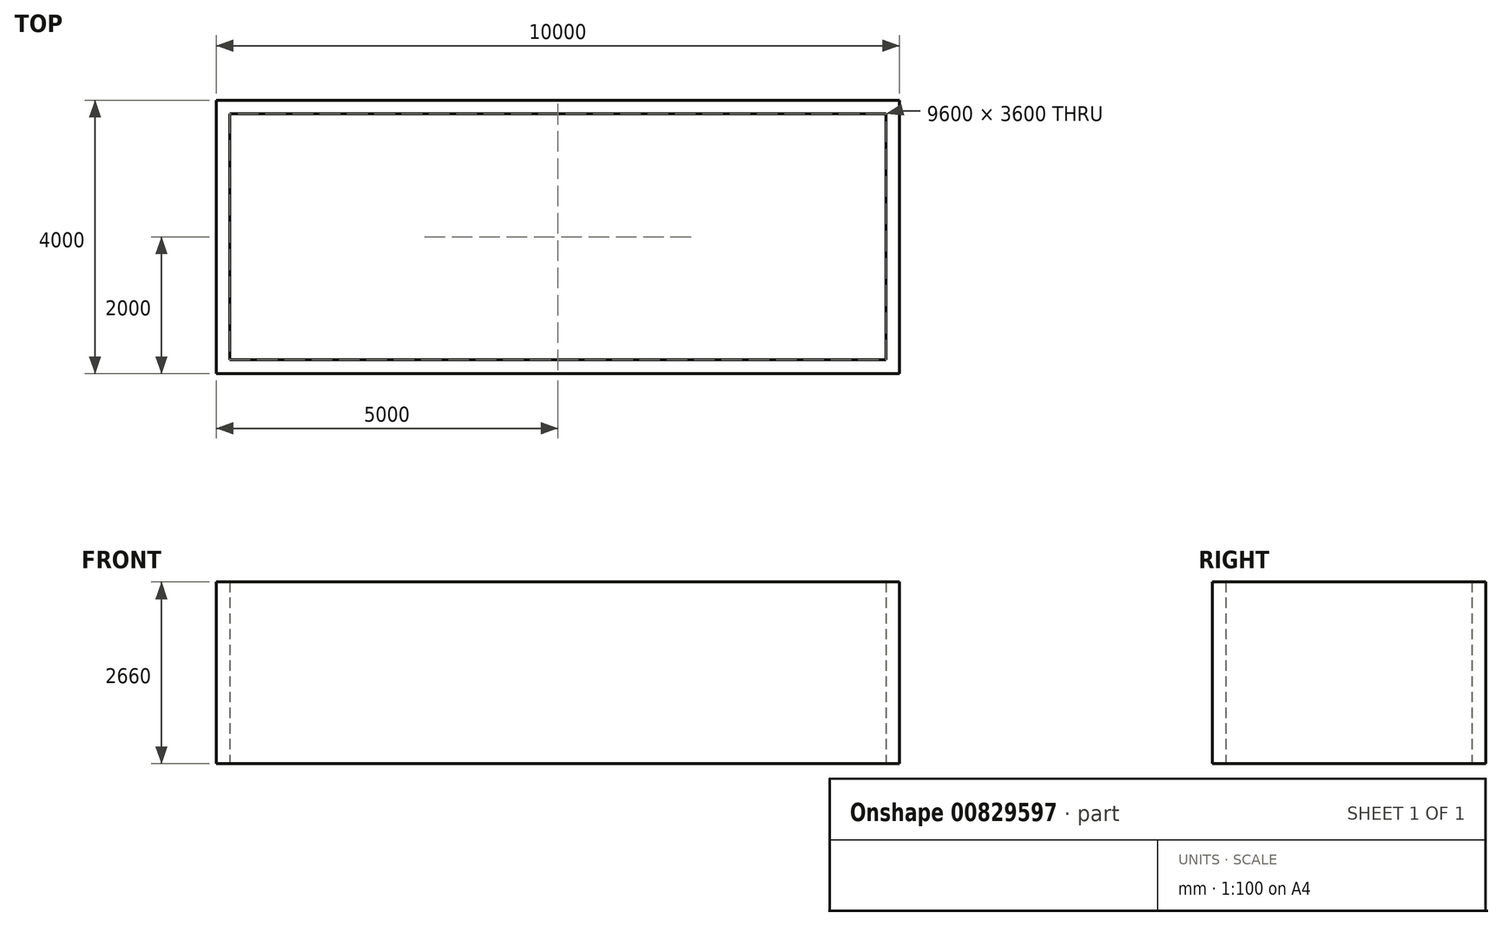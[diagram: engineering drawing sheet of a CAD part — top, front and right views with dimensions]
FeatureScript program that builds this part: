
annotation { "Feature Type Name" : "Feature", "Feature Type Description" : "" }
export const myFeature = defineFeature(function(context is Context, id is Id, definition is map)
    precondition{}
    {
        {
            var Q0;
            Q0=qCreatedBy(makeId("Top.planeOp"),FACE);
            var sketch = newSketch(context, id + "F0", { "sketchPlane" : qUnion([Q0])});
            skLineSegment(sketch, "E0.top", {"start": v(-9566.18, -2000) * mm, "end": v(433.82, -2000) * mm});
            skLineSegment(sketch, "E1", {"start": v(-9566.18, -2000) * mm, "end": v(-9566.18, 2000) * mm});
            skLineSegment(sketch, "E2", {"start": v(433.82, -2000) * mm, "end": v(433.82, 2000) * mm});
            skLineSegment(sketch, "E3", {"start": v(433.82, 2000) * mm, "end": v(-9566.18, 2000) * mm});
            skLineSegment(sketch, "E4.direction1", {"start": v(-9566.18, -2000) * mm, "end": v(-9366.18, -2000) * mm, "construction": true});
            skLineSegment(sketch, "E5.MirrorCS", {"start": v(-9366.18, -1800) * mm, "end": v(-9366.18, 1800) * mm});
            skLineSegment(sketch, "E6", {"start": v(-9566.18, 0) * mm, "end": v(-9366.18, 0) * mm});
            skLineSegment(sketch, "E7.MirrorCS", {"start": v(233.82, -1800) * mm, "end": v(233.82, 1800) * mm});
            skLineSegment(sketch, "E8", {"start": v(233.82, 1800) * mm, "end": v(-9366.18, 1800) * mm});
            skLineSegment(sketch, "E9", {"start": v(233.82, -1800) * mm, "end": v(-9366.18, -1800) * mm});
            skSolve(sketch);
        }
        {
            var Q0;
            Q0 = qSketchRegion(id + "F0", true);
            var Q1;
            {var subQ3=sQuery(id+"F0.wireOp",EDGE,"E0.top");Q1=makeQuery(id+"F0.imprint","IMPRINT",FACE,{"disambiguationData":[TD([[makeQuery(id+"F0.imprint","IMPRINT",EDGE,{"derivedFrom":subQ3}),1.0]])]});}
            extrude(context, id + "F1", {"entities" : qUnion([Q0, Q1]), "depth" : 2660 * mm, "offsetDistance" : 25 * mm});
        }
    });
